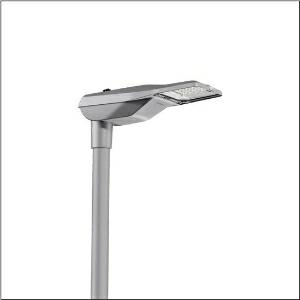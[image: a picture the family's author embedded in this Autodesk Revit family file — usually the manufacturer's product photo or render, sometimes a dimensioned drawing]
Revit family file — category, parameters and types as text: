
# Revit family: streetlight_sl_21_micro___pl52_5xe1h33s08db_2be5
name_source: partatom
category: Lighting Fixtures
units: mm (PartAtom-declared; Revit-internal decimal feet)

## family parameters
Cut with Voids When Loaded = No
Host = Face
Light Source = No
Part Type = Normal
Room Calculation Point = No
Round Connector Dimension = Use Diameter
Shared = No

## types (1)
- --- (1 x LED, 5020 lm, 39.1 W, 3000K)
    Apparent Load = 39 VA
    CIE Flux Codes = 27 59 98 100 100
    Color Rendering = 70
    Color Temperature = 3000K
    Default Elevation = 1800 mm
    Description = Streetlight SL 21 micro, mast luminaire, primary light control with lens, of PMMA, primary optical cover: cover, of toughened safety glass, transparent, light distribution: PL52, light emission: direct distribution, primary light characteristic: asymmetric, installation type: side-entry, post-top, LED, High Power LED, rated luminous flux: 5.020lm, luminous efficacy: 128lm/W, light colour: 730, colour temperature: 3000K, control gear: D4i, control: flexible luminous flux parameterisation, time-dependent luminous flux control, constant luminous flux control, overheat protection, pre-setting: logarithmic dimming characteristic, mains connection: 220..240V, AC, 50/60Hz, start of lifetime: 39W, end of service life: 41W, reduction: 18W, luminaire housing, of diecast aluminium, powder-coated, SITECO metallic grey (DB 702S), corrosivity category C5 high according to DIN EN ISO 12944, please order mast flange separately, inclination adjustable: 0°, 5°, 10°, 15°, sealing non-destructively replaceable, multi-level sealing system, length: 528mm, width: 235mm, height: 110mm, mast flange for spigot size: 42mm (side-entry): 5XC10008XM4, 60/48mm (side-entry/post-top): 5XC10108XM2, 76/60mm (side-entry/post-top): 5XC10108XM1, Smart Interface above, protection rating (complete): IP66, insulation class (complete): insulation class II (safety insulation), certification: CE, ENEC, ENEC+, VDE, impact resistance: IK10, permissible operating ambient temperature for outdoor applications: -40..+50°C, standard-compliant lighting for roads and squares, packaging unit: 1 piece

Light Distribution: PL52
    Height = 110 mm
    Lamp = 1 x LED
    Lamp Light Flux = 5020 lm
    Lamp Power = 39.1 W
    Lamp count = 1
    Length = 528 mm
    Luminous efficacy = 128 lm/W
    Manufacturer = Siteco
    ModVariant = No
    Model = 5XE1H33S08DB
    Number of Poles = 1
    OnlyDefault = Yes
    Power Factor = 1
    Product Name = Streetlight SL 21 micro | PL52
    Product group = mast luminaire | pylon top
    ProductGroupID = 6100
    Protection Class = Protection class II
    Protection Degree = IP 66
    RLX_Detail_Level = 1
    RLX_Emergency_Light_Flux = 0 lm
    RLX_Emergency_Type = 0
    RLX_Emergency_Type_DB = No
    RlxData = <blob elided: 108413 chars, md5=4ec09363>
    Socket = socket
    Standby Power = 0 W
    System Light Flux = 5020 lm
    System Power = 39 W
    Type Comments = factory setting: luminous flux: 100 % | dim-lin: 254 | 765 mA
    Type Image = l_1277292.jpg
    URL = http://relux.com
    VarID = @adj_155741
    Voltage = 0 V
    Weight = 0.00 kg
    Width = 235 mm

## geometry (parser evidence)
native form markers: Blend x4, Sweep x8
no freeform markers — native parametric forms only
